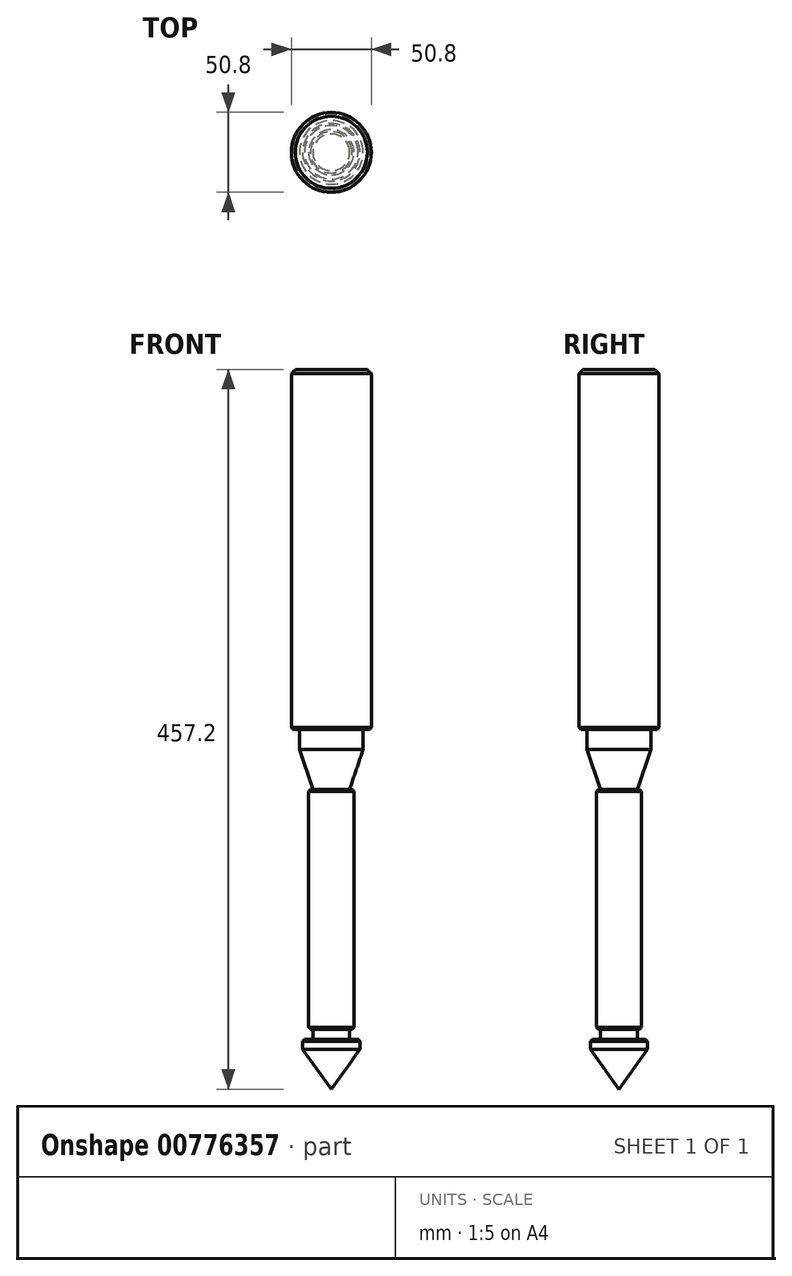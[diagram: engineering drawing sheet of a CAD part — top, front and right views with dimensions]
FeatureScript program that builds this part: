
annotation { "Feature Type Name" : "Feature", "Feature Type Description" : "" }
export const myFeature = defineFeature(function(context is Context, id is Id, definition is map)
    precondition{}
    {
        {
            var Q0;
            Q0=qCreatedBy(makeId("Front.planeOp"),FACE);
            var sketch = newSketch(context, id + "F0", { "sketchPlane" : qUnion([Q0])});
            skLineSegment(sketch, "E0.top", {"start": v(0, 228.6) * mm, "end": v(-25.4, 228.6) * mm});
            skPoint(sketch, "E0.middle", {"position": v(0, 0) * mm});
            skLineSegment(sketch, "E1", {"start": v(-25.4, 228.6) * mm, "end": v(-25.4, 0) * mm});
            skLineSegment(sketch, "E2", {"start": v(-25.4, 0) * mm, "end": v(-20.22, 0) * mm});
            skLineSegment(sketch, "E3", {"start": v(-20.22, 0) * mm, "end": v(-20.22, -12.7) * mm});
            skLineSegment(sketch, "E4", {"start": v(-20.22, -12.7) * mm, "end": v(-11.67, -38.1) * mm});
            skLineSegment(sketch, "E5", {"start": v(-11.67, -38.1) * mm, "end": v(-14.37, -38.1) * mm});
            skLineSegment(sketch, "E6", {"start": v(-14.37, -38.1) * mm, "end": v(-14.37, -190.5) * mm});
            skLineSegment(sketch, "E7", {"start": v(-14.37, -190.5) * mm, "end": v(-11.67, -190.5) * mm});
            skLineSegment(sketch, "E8", {"start": v(-11.67, -190.5) * mm, "end": v(-11.67, -196.85) * mm});
            skLineSegment(sketch, "E9", {"start": v(-11.67, -196.85) * mm, "end": v(-18.24, -196.85) * mm});
            skLineSegment(sketch, "E10", {"start": v(-18.24, -196.85) * mm, "end": v(-18.24, -203.2) * mm});
            skLineSegment(sketch, "E11", {"start": v(-18.24, -203.2) * mm, "end": v(0, -228.6) * mm});
            skLineSegment(sketch, "E12", {"start": v(0, 228.6) * mm, "end": v(0, -228.6) * mm});
            skPoint(sketch, "E13.end.orphan", {"position": v(0, -38.1) * mm});
            skSolve(sketch);
        }
        {
            var Q0;
            Q0=makeQuery(id+"F0.imprint","IMPRINT",FACE,{"disambiguationData":[TD([[makeQuery(id+"F0.imprint","IMPRINT",EDGE,{"derivedFrom":sQuery(id+"F0.wireOp",EDGE,"E0.top")}),1.0]])]});
            var Q1;
            Q1=sQuery(id+"F0.wireOp",EDGE,"E12");
            revolve(context, id + "F1", {"surfaceOperationType" : NewSurfaceOperationType.NEW, "entities" : qUnion([Q0]), "axis" : qUnion([Q1]), "revolveType" : RevolveType.FULL});
        }
        {
            var Q0;
            Q0=makeQuery(id+"F1.opRevolve","SWEPT_EDGE",EDGE,{"disambiguationData":[OSD([sQuery(id+"F0.wireOp",EDGE,"E0.top"),sQuery(id+"F0.wireOp",EDGE,"E1")])]});
            chamfer(context, id + "F2", {"entities" : qUnion([Q0]), "width" : 2.54 * mm, "tangentPropagation" : true});
        }
        {
            var Q0;
            Q0=makeQuery(id+"F1.opRevolve","SWEPT_EDGE",EDGE,{"disambiguationData":[OSD([sQuery(id+"F0.wireOp",EDGE,"E1"),sQuery(id+"F0.wireOp",EDGE,"E2")])]});
            var Q1;
            Q1=makeQuery(id+"F1.opRevolve","SWEPT_EDGE",EDGE,{"disambiguationData":[OSD([sQuery(id+"F0.wireOp",EDGE,"E5"),sQuery(id+"F0.wireOp",EDGE,"E6")])]});
            var Q2;
            Q2=makeQuery(id+"F1.opRevolve","SWEPT_EDGE",EDGE,{"disambiguationData":[OSD([sQuery(id+"F0.wireOp",EDGE,"E9"),sQuery(id+"F0.wireOp",EDGE,"E10")])]});
            var Q3;
            Q3=makeQuery(id+"F1.opRevolve","SWEPT_EDGE",EDGE,{"disambiguationData":[OSD([sQuery(id+"F0.wireOp",EDGE,"E6"),sQuery(id+"F0.wireOp",EDGE,"E7")])]});
            chamfer(context, id + "F3", {"entities" : qUnion([Q0, Q1, Q2, Q3]), "width" : 1.27 * mm, "tangentPropagation" : true});
        }
    });
